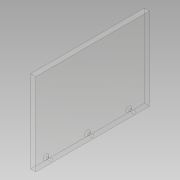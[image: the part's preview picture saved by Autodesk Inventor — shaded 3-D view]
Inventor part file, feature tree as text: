
AUTODESK INVENTOR PART (.ipt)
format: ipt  version: 2019 (Build 230136000, 136)  size: 93,184 bytes
history: native  units: mm
features: sketch x2, other x1, extrude x1, hole x1
ambient origin geometry x8: Origin, YZ Plane, XZ Plane, XY Plane, X Axis, Y Axis, Z Axis, Center Point
bodies: Body1 (feature_tree)
feature tree (5):
  other  "Sólido1"
  extrude  "Extrusión1"  Depth=220.0mm
  hole  "Agujero1"  [1 undecoded]
  sketch  "Boceto1"  dims[d0=160.0mm d1=220.0mm]
  sketch  "Boceto2"  dims[d2=10.0mm d3=0.0mm d7=5.5mm d8=6.0mm d9=11.0mm d10=2.0mm d11=90.0deg d12=20.0mm d13=20.594885mm]
note: 1 required parameter value undecoded (feature->parameter linkage not recoverable at this tier; creation-order binding heuristic only, values carry confidence <= 0.55)
